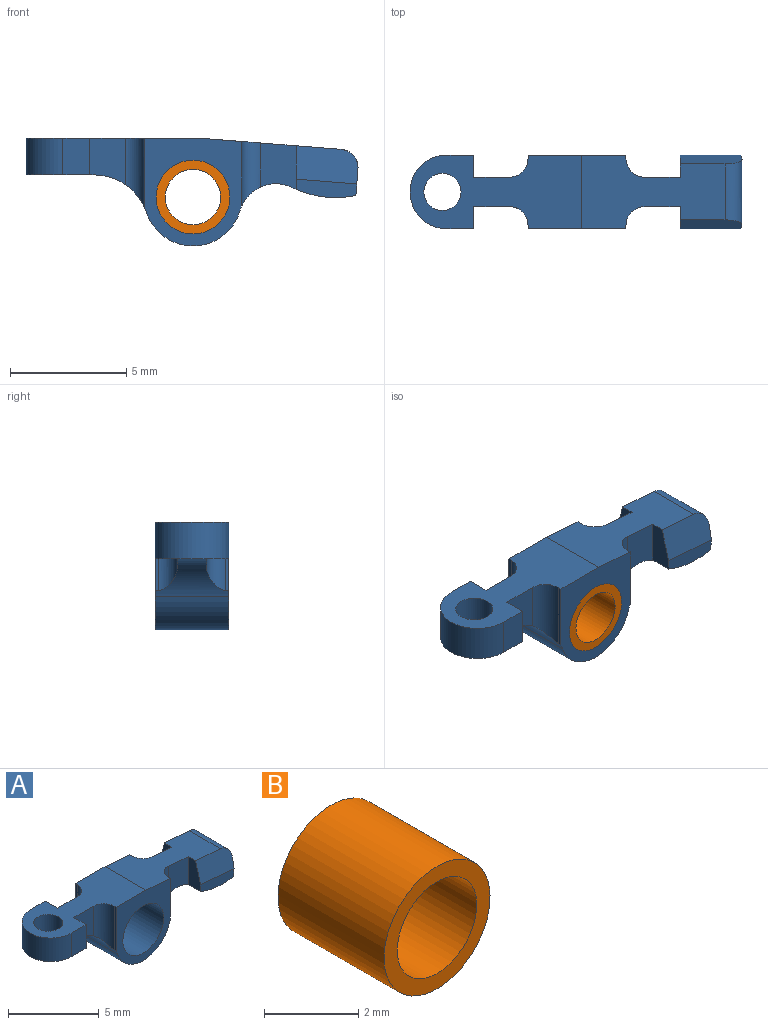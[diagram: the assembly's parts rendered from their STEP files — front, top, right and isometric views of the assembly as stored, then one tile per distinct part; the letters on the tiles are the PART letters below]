
ASSEMBLY  parts=2 mates=1
PART A: 36 faces, bbox 14.3x3.2x4.7 mm
  f0: plane 6.2x3.2mm, normal (0.08,0,1), area 14mm2, adj f2,f3,f4,f10,f11,f17,f18,f19
  f1: plane 3.18x1.14mm, normal (1,0,-0.08), area 3.5mm2, adj f8,f15,f16,f27,f28,f34
  f2: plane 1.89x0.95mm, normal (-1,0,0), area 1.5mm2, adj f0,f8,f15,f17,f28
  f3: plane 1.89x0.95mm, normal (-1,0,0), area 1.5mm2, adj f0,f8,f16,f20,f27
  f4: plane 7.39x3.18mm, normal (0,0,1), area 16.2mm2, adj f0,f9,f10,f11,f12,f21,f22,f23
  f5: plane 3.18x2.93mm, normal (0,0,-1), area 5.9mm2, adj f6,f9,f12,f21,f22,f24,f25,f29
  f6: cylinder r=2.38mm len=3.18mm, axis (0,1,0), area 4.8mm2, adj f5,f10,f11,f13,f21,f23,f24,f26
  f7: cylinder r=1.59mm len=3.18mm, axis (0,1,0), area 4.5mm2, adj f8,f10,f11,f13,f17,f18,f19,f20
  f8: cylinder r=4.32mm len=3.18mm, axis (0,1,0), area 8.6mm2, adj f1,f2,f3,f7,f15,f16,f17,f20
  f9: plane 1.59x1.16mm, normal (0,-1,0), area 1.8mm2, adj f4,f5,f25,f35
  f10: plane 4.65x4.22mm, normal (0,-1,0), area 9.6mm2, adj f0,f4,f6,f7,f13,f14,f18,f26
  f11: plane 4.65x4.22mm, normal (0,1,0), area 9.6mm2, adj f0,f4,f6,f7,f13,f14,f19,f23
  f12: plane 1.59x1.16mm, normal (0,1,0), area 1.8mm2, adj f4,f5,f22,f35
  f13: cylinder r=2.11mm len=4.03mm, axis (0,1,0), area 17mm2, adj f6,f7,f10,f11
  f14: cylinder r=1.59mm len=3.18mm, axis (0,1,0), area 31.7mm2, adj f10,f11
  f15: plane 2.61x0.8mm, normal (0,-1,0), area 1.6mm2, adj f1,f2,f8,f28
  f16: plane 2.61x0.8mm, normal (0,1,0), area 1.6mm2, adj f1,f3,f8,f27
  f17: plane 2.01x1.54mm, normal (0,-1,0), area 2.7mm2, adj f0,f2,f7,f8,f30
  f18: plane 2.75x0.16mm, normal (1,0,0), area 0.4mm2, adj f0,f7,f10,f30
  f19: plane 2.75x0.16mm, normal (1,0,0), area 0.4mm2, adj f0,f7,f11,f31
  f20: plane 2.01x1.54mm, normal (0,1,0), area 2.7mm2, adj f0,f3,f7,f8,f31
  f21: plane 2.01x1.54mm, normal (0,1,0), area 2.6mm2, adj f4,f5,f6,f22,f33
  f22: plane 1.59x0.95mm, normal (1,0,0), area 1.5mm2, adj f4,f5,f12,f21
  f23: plane 2.94x0.16mm, normal (-1,0,0), area 0.5mm2, adj f4,f6,f11,f33
  f24: plane 2.01x1.54mm, normal (0,-1,0), area 2.6mm2, adj f4,f5,f6,f25,f32
  f25: plane 1.59x0.95mm, normal (1,0,0), area 1.5mm2, adj f4,f5,f9,f24
  f26: plane 2.94x0.16mm, normal (-1,0,0), area 0.5mm2, adj f4,f6,f10,f32
  f27: plane 2.66x1.64mm, normal (0.02,0.97,0.26), area 3.8mm2, adj f0,f1,f3,f16,f34
  f28: plane 2.66x1.64mm, normal (0.02,-0.97,0.26), area 3.8mm2, adj f0,f1,f2,f15,f34
  f29: cylinder r=0.8mm len=1.6mm, axis (0,0,1), area 8mm2, adj f4,f5
  f30: cylinder r=0.79mm len=2.75mm, axis (0,0,-1), area 2.9mm2, adj f0,f7,f17,f18
  f31: cylinder r=0.79mm len=2.75mm, axis (0,0,-1), area 2.9mm2, adj f0,f7,f19,f20
  f32: cylinder r=0.79mm len=2.94mm, axis (0,0,-1), area 3.2mm2, adj f4,f6,f24,f26
  f33: cylinder r=0.79mm len=2.94mm, axis (0,0,-1), area 3.2mm2, adj f4,f6,f21,f23
  f34: cylinder r=0.79mm len=2.83mm, axis (0,1,0), area 3.2mm2, adj f0,f1,f27,f28
  f35: cylinder r=1.59mm len=3.18mm, axis (0,0,1), area 7.9mm2, adj f4,f5,f9,f12
PART B: 4 faces, bbox 3.2x3.2x3.2 mm
  f0: cylinder r=1.19mm len=3.18mm, axis (0,1,0), area 23.8mm2, adj f2,f3
  f1: cylinder r=1.59mm len=3.18mm, axis (0,1,0), area 31.7mm2, adj f2,f3
  f2: plane 3.18x3.18mm, normal (0,-1,0), area 3.5mm2, adj f0,f1
  f3: plane 3.18x3.18mm, normal (0,1,0), area 3.5mm2, adj f0,f1
PLACE A at identity fixed
PLACE B at identity
MATE fastened B.f0 <-> A.f14  axis (0,1,0) through (0,-1.59,0)mm
